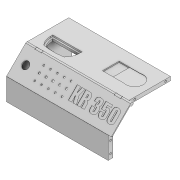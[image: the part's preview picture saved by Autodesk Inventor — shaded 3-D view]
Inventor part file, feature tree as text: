
AUTODESK INVENTOR PART (.ipt)
format: ipt  version: 2020 (Build 240168000, 168)  size: 1,100,288 bytes
history: native  units: mm
features: sketch x31, extrude x28, projected_geometry x20, chamfer x3, plane x3, emboss x1
ambient origin geometry x8: Origin, YZ Plane, XZ Plane, XY Plane, X Axis, Y Axis, Z Axis, Center Point
bodies: Solid1 (feature_tree)
feature tree (86):
  extrude  "Extrusion1"  Depth=120.0mm
  extrude  "Extrusion2"  Depth=40.0mm
  extrude  "Extrusion3"  TaperAngle=135.0deg  [1 undecoded]
  extrude  "Extrusion4"  Depth=125.0mm
  extrude  "Extrusion5"  Depth=1.0mm
  extrude  "Extrusion6"  Depth=20.0mm
  extrude  "Extrusion7"  Depth=10.0mm TaperAngle=0.0deg
  extrude  "Extrusion8"  Depth=3.0mm
  extrude  "Extrusion9"  Depth=0.25mm
  extrude  "Extrusion10"  Depth=0.25mm
  extrude  "Extrusion11"  Depth=0.3mm
  extrude  "Extrusion17"  Depth=20.0mm TaperAngle=0.0deg
  extrude  "Extrusion18"  Depth=14.196mm
  extrude  "Extrusion19"  Depth=0.35mm TaperAngle=0.0deg
  extrude  "Extrusion20"  Depth=19.547688mm
  extrude  "Extrusion21"  Depth=0.3mm
  extrude  "Extrusion22"  Depth=0.3mm
  extrude  "Extrusion23"  Depth=0.3mm
  extrude  "Extrusion24"  Depth=0.3mm
  sketch  "Sketch25"  dims[d73=0.3mm d74=5.0mm d75=0.25mm d76=19.547688mm d77=0.35mm d78=0.0mm]
  chamfer  "Chamfer1"  Distance=20.0mm
  chamfer  "Chamfer2"  Distance=0.35mm
  sketch  "Sketch26"  dims[d79=0.3mm d80=5.0mm d81=0.25mm d82=19.547688mm d83=20.0mm d84=0.0mm]
  extrude  "Extrusion25"  Depth=20.0mm TaperAngle=0.0deg
  emboss  "Emboss1"
  plane  "Work Plane1"
  extrude  "Extrusion26"  Depth=10.0mm TaperAngle=0.0deg
  plane  "Work Plane2"
  extrude  "Extrusion27"  Depth=10.0mm TaperAngle=0.0deg
  plane  "Work Plane3"
  extrude  "Extrusion28"  Depth=10.0mm
  extrude  "Extrusion29"  Depth=10.0mm
  chamfer  "Chamfer3"  Distance=10.0mm
  extrude  "Extrusion30"  Depth=15.0mm
  extrude  "Extrusion31"  Depth=15.0mm
  extrude  "Extrusion32"  Depth=6.0mm
  extrude  "Extrusion33"  Depth=15.0mm
  sketch  "Sketch1"  dims[d0=55.0mm d1=120.0mm]
  sketch  "Sketch2"  dims[d2=50.0mm d3=40.0mm]
  projected_geometry  "Projected Loop1"
  sketch  "Sketch3"  dims[d4=135.0deg d5=135.0deg]
  sketch  "Sketch4"  dims[d6=5.0mm d7=125.0mm]
  projected_geometry  "Projected Loop2"
  projected_geometry  "Projected Loop3"
  sketch  "Sketch5"  dims[d8=190.0mm d9=1.0mm]
  sketch  "Sketch6"  dims[d10=1.0mm d11=20.0mm]
  sketch  "Sketch7"  dims[d12=3.0mm d13=10.0mm d14=0.0mm]
  sketch  "Sketch8"  dims[d15=3.0mm d16=0.3mm]
  sketch  "Sketch9"  dims[d18=5.0mm d19=0.25mm]
  sketch  "Sketch10"  dims[d21=0.25mm d22=0.25mm]
  sketch  "Sketch11"  dims[d23=0.0mm d24=0.0mm d25=0.3mm d26=5.0mm d27=0.25mm]
  sketch  "Sketch17"  dims[d28=2.0mm d29=20.0mm d30=0.0mm]
  projected_geometry  "Projected Loop7"
  sketch  "Sketch18"  dims[d36=5.0mm d37=14.196mm]
  sketch  "Sketch19"  dims[d38=0.3mm d39=5.0mm d40=0.25mm d41=0.35mm d42=0.0mm]
  projected_geometry  "Projected Loop8"
  sketch  "Sketch20"  dims[d43=0.3mm d44=5.0mm d45=0.25mm d46=19.547688mm]
  sketch  "Sketch21"  dims[d47=20.0mm d48=0.0mm d49=0.3mm d50=5.0mm d51=0.25mm d52=19.547688mm]
  projected_geometry  "Projected Loop9"
  projected_geometry  "Projected Loop10"
  sketch  "Sketch22"  dims[d53=0.35mm d54=0.0mm d55=0.3mm d56=5.0mm d57=0.25mm d58=19.547688mm]
  projected_geometry  "Projected Loop11"
  projected_geometry  "Projected Loop12"
  projected_geometry  "Projected Loop13"
  projected_geometry  "Projected Loop14"
  sketch  "Sketch23"  dims[d59=228.6mm d60=0.0mm d61=0.3mm d62=5.0mm d63=0.25mm d64=19.547688mm]
  sketch  "Sketch24"  dims[d65=0.35mm d66=0.0mm d67=0.3mm d68=5.0mm d69=0.25mm d70=19.547688mm d71=20.0mm d72=0.0mm]
  projected_geometry  "Projected Loop15"
  projected_geometry  "Projected Loop16"
  projected_geometry  "Projected Loop17"
  projected_geometry  "Projected Loop18"
  projected_geometry  "Projected Loop19"
  projected_geometry  "Projected Loop20"
  sketch  "Sketch27"  dims[d96=3.0mm d107=10.0mm d108=0.0mm]
  sketch  "Sketch28"  dims[d109=12.0mm d110=10.0mm d111=0.0mm]
  sketch  "Sketch29"  dims[d112=10.0mm d113=0.0mm d114=12.0mm]
  sketch  "Sketch30"  dims[d115=5.5mm d116=3.25mm d117=10.0mm d118=0.0mm]
  projected_geometry  "Projected Loop21"
  sketch  "Sketch31"  dims[d119=6.0mm d120=15.0mm]
  projected_geometry  "Projected Loop22"
  sketch  "Sketch32"  dims[d121=6.0mm d122=15.0mm]
  sketch  "Sketch33"  dims[d123=6.0mm d124=6.0mm]
  sketch  "Sketch34"  dims[d125=15.0mm d126=15.0mm]
  projected_geometry  "Projected Loop23"
  sketch  "Sketch35"  dims[d127=4.0mm d128=0.0mm]
  sketch  "Sketch36"  dims[d129=4.2mm d130=4.2mm d131=4.2mm d132=4.2mm d133=3.0mm d134=0.0mm d135=6.0mm d136=6.0mm d137=15.0mm d138=15.0mm d139=4.0mm d140=0.0mm d141=4.2mm d142=4.2mm d143=3.0mm d144=0.0mm d145=2.0mm d146=4.0mm d147=45.0deg d148=2.0mm d149=4.0mm d150=45.0deg d151=22.2mm d152=6.4mm d153=6.4mm d154=6.4mm d155=6.4mm d156=6.4mm d157=30.0mm d158=40.0mm d159=43.2mm d160=21.4mm d161=21.4mm d162=21.4mm d163=21.4mm d164=10.0mm d165=13.2mm d166=0.0mm d167=0.0mm d168=5.1mm d169=5.1mm d170=5.1mm d171=5.1mm d172=5.1mm d173=3.0mm d174=0.0mm d175=22.2mm d176=6.4mm d177=6.4mm d178=6.4mm d179=6.4mm d180=6.4mm d181=30.0mm d182=40.0mm d183=43.2mm d184=21.4mm d185=21.4mm d186=21.4mm d187=21.4mm d188=10.0mm d189=13.2mm d190=0.0mm d191=0.0mm d192=5.1mm d193=5.1mm d194=5.1mm d195=5.1mm d196=5.1mm d197=1.0mm d198=0.0mm d199=5.2mm d200=50.0mm d201=6.0mm d202=10.0mm d203=3.0mm d204=10.0mm d205=0.0mm d206=160.0mm d207=10.0mm d208=0.0mm d209=266.0mm d210=10.0mm d211=0.0mm d212=6.0mm d213=6.0mm d214=6.0mm d215=10.0mm d216=0.0mm d217=10.0mm d218=4.0mm d219=45.0deg d299=27.0mm d300=67.21989mm d301=67.21989mm d302=52.0mm d303=74.5mm d304=26.0mm d305=26.0mm d306=121.0mm d307=0.25mm d308=0.25mm d309=0.25mm d310=0.25mm d311=3.5mm d312=0.0mm d313=32.75mm d314=2.5mm d315=0.0mm d316=72.0mm d317=91.999999mm d318=81.999999mm d319=167.166667mm d320=45.750001mm d321=45.750001mm d322=50.750001mm d323=172.166667mm d324=50.750001mm d325=7.0mm d326=7.0mm d327=2.0mm d328=2.0mm d329=5.0mm d330=32.384967mm d331=32.384967mm d332=22.0mm d333=0.15mm d334=5.0mm d335=0.0mm d336=72.0mm d337=91.999999mm d338=81.999999mm d339=167.166667mm d340=45.750001mm d341=45.750001mm d342=50.750001mm d343=172.166667mm d344=50.750001mm d345=7.0mm d346=7.0mm d347=2.0mm d348=2.0mm d349=5.0mm d350=32.384967mm d351=32.384967mm d352=22.0mm d353=0.15mm d354=5.0mm d355=0.0mm d17=0.872665mm]
note: 1 required parameter value undecoded (feature->parameter linkage not recoverable at this tier; creation-order binding heuristic only, values carry confidence <= 0.55)
